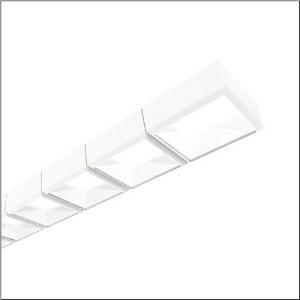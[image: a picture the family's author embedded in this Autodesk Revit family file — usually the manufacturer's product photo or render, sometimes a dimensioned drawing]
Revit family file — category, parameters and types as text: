
# Revit family: scriptus_11_5mz223d04wa
name_source: partatom
category: Lighting Fixtures
units: mm (PartAtom-declared; Revit-internal decimal feet)

## family parameters
Cut with Voids When Loaded = No
Host = Face
Light Source = No
Part Type = Normal
Room Calculation Point = No
Round Connector Dimension = Use Diameter
Shared = No

## types (1)
- --- (1 x LED 4000K / CRI = 80 (unbekannt), 7230 lm, 4000K)
    Apparent Load = 51 VA
    CIE Flux Codes = 82 95 99 100 100
    Color Rendering = 80
    Color Temperature = 4000K
    Default Elevation = 1800 mm
    Description = Scriptus 11, office luminaire, primary optical cover: lenses, CAT 2 (L<= 3000cd/m²), light emission: direct distribution, primary light characteristic: symmetric, installation type: surface-mounted, LED, rated luminous flux: 7.230lm, luminous efficacy: 143lm/W, light colour: 840, colour temperature: 4000K, control gear: DALI, with terminal, 5-pole, mains connection: 230V, AC, 50Hz, rated input power: 51W, housing, luminaire housing, of aluminium, traffic white (RAL 9016), length: 2.426mm, width: 114mm, height: 57mm, protection rating (complete): IP20, insulation class (complete): insulation class I (protective earthing), certification: CE, ENEC, VDE, protection symbol: F, permissible operating ambient temperature: 0..+35°C, standard: EN 50419, packaging unit: 1 piece
    Height = 57 mm
    Lamp = 1 x LED 4000K / CRI >= 80 (unbekannt)
    Lamp Light Flux = 7230 lm
    Lamp count = 1
    Length = 2426 mm
    Luminous efficacy = 143 lm/W
    Manufacturer = Siteco
    ModVariant = No
    Model = 5MZ223D04WA
    Mounting Place = Ceiling
    Mounting Type = Surface mounted
    Number of Poles = 1
    OnlyDefault = Yes
    Power Factor = 1
    Product Name = Scriptus 11
    Product group = office luminaire | ceiling mounted
    ProductGroupID = 301
    Protection Class = Protection class I
    Protection Degree = IP 20
    RLX_Detail_Level = 1
    RLX_Emergency_Light_Flux = 0 lm
    RLX_Emergency_Type = 0
    RLX_Emergency_Type_DB = No
    RlxData = <blob elided: 31325 chars, md5=9f1372c5>
    Socket = socket
    Standby Power = 0 W
    System Light Flux = 7230 lm
    System Power = 51 W
    Type Comments = factory setting: luminous flux: 100 % | dim-lin: 254 | 525 mA
    Type Image = l_1004833.jpg
    URL = http://relux.com
    VarID = @adj_196331
    Voltage = 0 V
    Weight = 0.00 kg
    Width = 114 mm

## geometry (parser evidence)
native form markers: Blend x4, Sweep x9
no freeform markers — native parametric forms only
